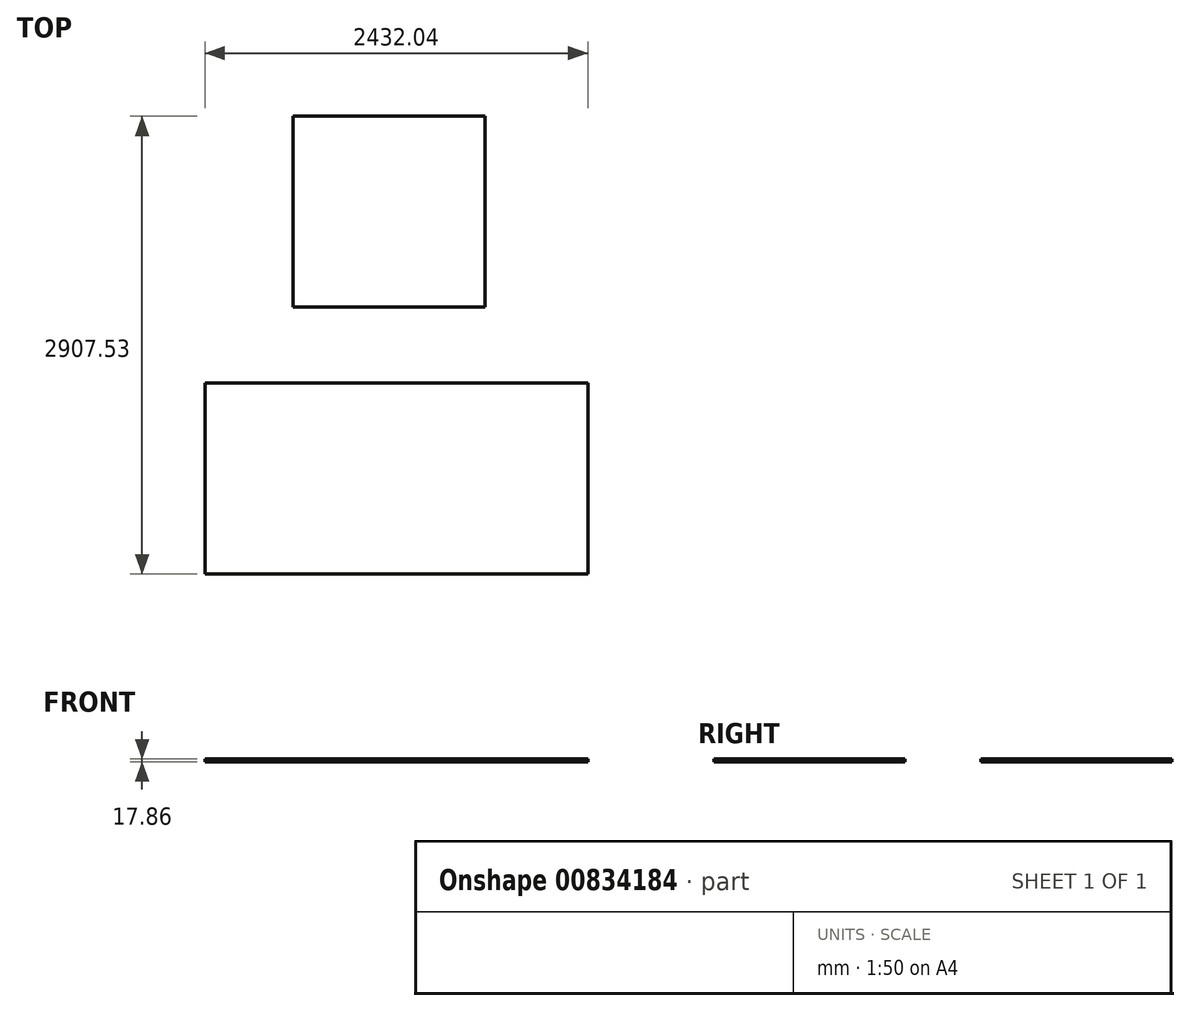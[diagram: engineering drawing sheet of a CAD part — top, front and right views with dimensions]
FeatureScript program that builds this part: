
annotation { "Feature Type Name" : "Feature", "Feature Type Description" : "" }
export const myFeature = defineFeature(function(context is Context, id is Id, definition is map)
    precondition{}
    {
        {
            var Q0;
            Q0=qCreatedBy(makeId("Top.planeOp"),FACE);
            var sketch = newSketch(context, id + "F0", { "sketchPlane" : qUnion([Q0])});
            skLineSegment(sketch, "E0.bottom", {"start": v(1216.03, -606.43) * mm, "end": v(-1216.03, -606.43) * mm});
            skLineSegment(sketch, "E0.top", {"start": v(1216.02, 606.43) * mm, "end": v(-1216.03, 606.42) * mm});
            skLineSegment(sketch, "E0.left", {"start": v(1216.03, -606.43) * mm, "end": v(1216.03, 606.43) * mm});
            skLineSegment(sketch, "E0.right", {"start": v(-1216.02, -606.43) * mm, "end": v(-1216.03, 606.42) * mm});
            skPoint(sketch, "E0.middle", {"position": v(0, 0) * mm});
            skLineSegment(sketch, "E1.bottom", {"start": v(-657.46, 1088.26) * mm, "end": v(561.74, 1088.26) * mm});
            skLineSegment(sketch, "E1.top", {"start": v(-657.46, 2301.1) * mm, "end": v(561.74, 2301.1) * mm});
            skLineSegment(sketch, "E1.left", {"start": v(-657.46, 1088.26) * mm, "end": v(-657.46, 2301.1) * mm});
            skLineSegment(sketch, "E1.right", {"start": v(561.74, 1088.26) * mm, "end": v(561.74, 2301.1) * mm});
            skPoint(sketch, "E1.middle", {"position": v(-47.86, 1694.68) * mm});
            skSolve(sketch);
        }
        {
            var Q0;
            Q0=makeQuery(id+"F0.imprint","IMPRINT",FACE,{"disambiguationData":[TD([[makeQuery(id+"F0.imprint","IMPRINT",EDGE,{"derivedFrom":sQuery(id+"F0.wireOp",EDGE,"E0.bottom")}),-1.0]])]});
            extrude(context, id + "F1", {"entities" : qUnion([Q0]), "depth" : 17.86 * mm, "offsetDistance" : 25.4 * mm});
        }
        {
            var Q0;
            Q0=makeQuery(id+"F0.imprint","IMPRINT",FACE,{"disambiguationData":[TD([[makeQuery(id+"F0.imprint","IMPRINT",EDGE,{"derivedFrom":sQuery(id+"F0.wireOp",EDGE,"E1.bottom")}),1.0]])]});
            extrude(context, id + "F2", {"entities" : qUnion([Q0]), "depth" : 17.86 * mm, "offsetDistance" : 25.4 * mm});
        }
    });
